# Revit family: LAMP_SHOT 290 G2
name_source: partatom
category: Modelos genéricos
revit_build: Autodesk Revit 2018 (Build: 20190510_1515(x64)
units: mm (PartAtom-declared; Revit-internal decimal feet)

## family parameters
Anfitrión = Cara
Compartido = No
Corte con vacíos al cargar = No
Cota de conector redondo = Diámetro de uso
Puede alojar armadura = No
Punto de cálculo de habitación = No
Tipo de pieza = Normal

## types (6) — shared parameters
CRI = 80
Comentarios de tipo = Availability of tilting between -50º and 215º when placed in a project.
Elevación por defecto = 1219 mm
Fabricante = LAMP
Finish = Texturised grey
Gear = Electronic
IEE = A+
Installation instructions = http://www.lamp.es
Insulation class = I
LED Lifetime = 60.000 L80 B10
Lamp = HIGH POWER LED
Last update = 21/02/2022
Luminaire type = Outdoor - Spotlight
MacAdam = 4
Manufacturer URL = http://www.lamp.es
Manufacturer country = Spain
Manufacturer name = LAMP
Model explanation = Availability of tilting between -50º and 215º when placed in a project.
Plum = 48 W
Power = 44 W
Power Supply = 220-240V 50/60Hz
Product URL = http://www.lamp.es
Product datasheet = http://www.lamp.es
Protection rating = IP65 / IK08
Type = HI POWER PHILIPS
Weight = 8.61 kg

## per-type parameters (varying)
| type | Descripción | Efficacy | Initial color | Initial intensity | Modelo | Photometric web file | Product code |
| 4011LM 3000 SPOT | SHOT 290 G2 6500 8WW SP GR. | 84 lm/W | 3000 K | 4011 lm | SH22965SP830NG | Cabeza Shot : 4011LM 3000 SPOT | SH22965SP830NG |
| 4068LM 3000 MEDIUM FLOOD | SHOT 290 G2 6500 8WW MFL GR. | 85 lm/W | 3000 K | 4068 lm | SH22965MF830NG | Cabeza Shot : 4068LM 3000 MEDIUM FLOOD | SH22965MF830NG |
| 4179LM 3000 STREET | SHOT 290 G2 6500 8WW STREET GR. | 87 lm/W | 3000 K | 4179 lm | SH22965ST830NG | Cabeza Shot : 4179LM 3000 STREET | SH22965ST830NG |
| 4223LM 4000 SPOT | SHOT 290 G2 6500 8NW SP GR. | 88 lm/W | 4000 K | 4223 lm | SH22965SP840NG | Cabeza Shot : 4223LM 4000 SPOT | SH22965SP840NG |
| 4282LM 4000 MEDIUM FLOOD | SHOT 290 G2 6500 8NW MFL GR. | 89 lm/W | 4000 K | 4282 lm | SH22965MF840NG | Cabeza Shot : 4282LM 4000 MEDIUM FLOOD | SH22965MF840NG |
| 4400LM 4000 STREET | SHOT 290 G2 6500 8NW STREET GR. | 92 lm/W | 4000 K | 4400 lm | SH22965ST840NG | Cabeza Shot : 4400LM 4000 STREET | SH22965ST840NG |
